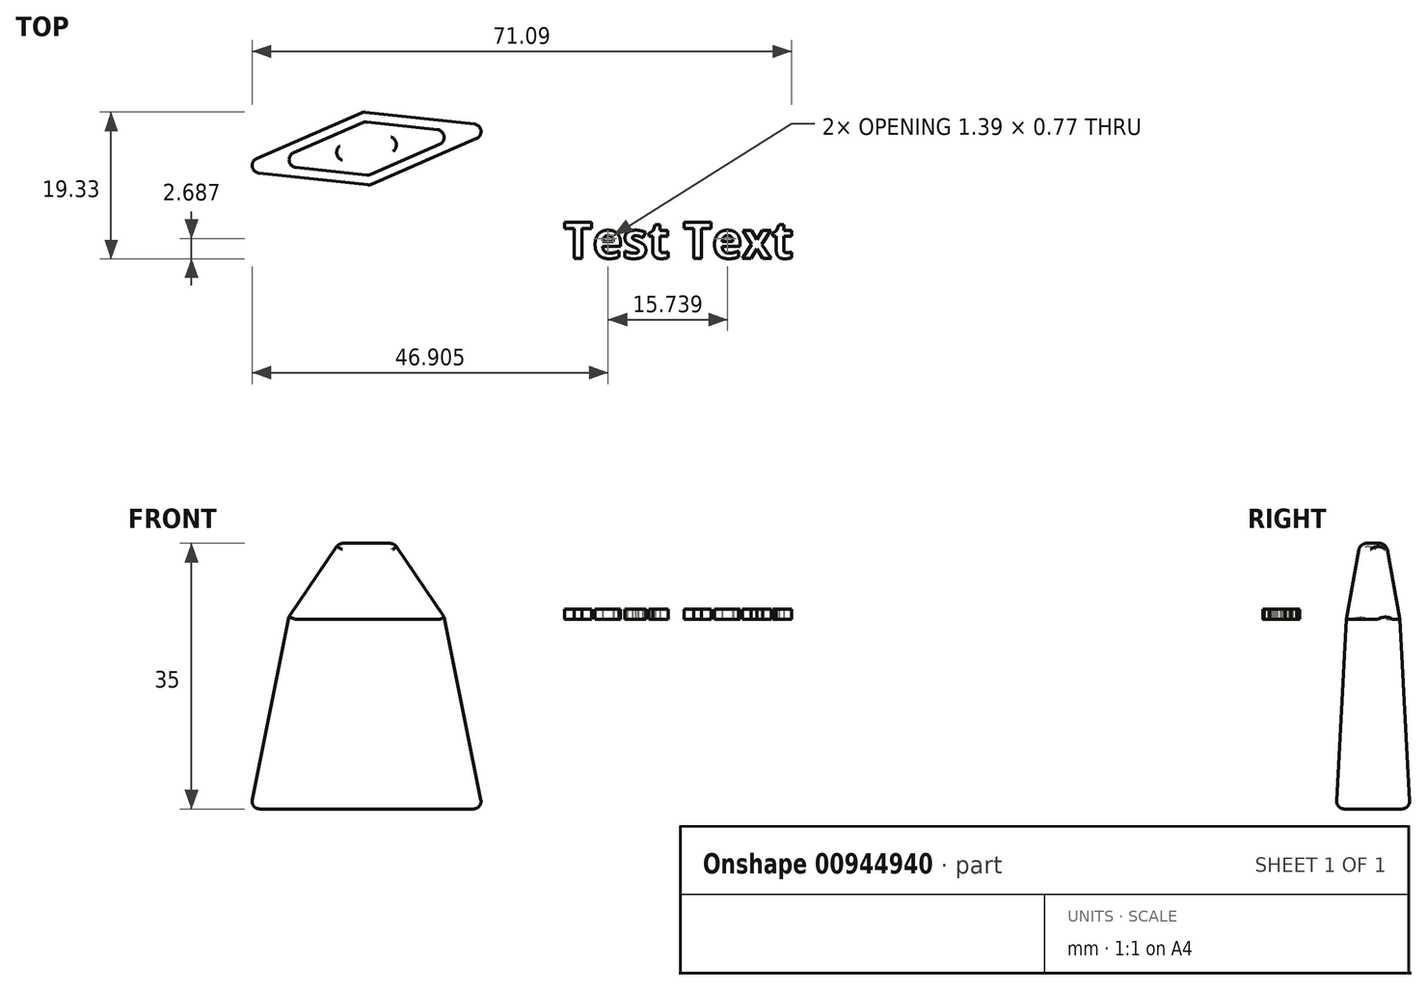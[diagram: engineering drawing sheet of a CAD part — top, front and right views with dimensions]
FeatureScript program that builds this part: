
annotation { "Feature Type Name" : "Feature", "Feature Type Description" : "" }
export const myFeature = defineFeature(function(context is Context, id is Id, definition is map)
    precondition{}
    {
        {
            var Q0;
            Q0=qCreatedBy(makeId("Top.planeOp"),FACE);
            var sketch = newSketch(context, id + "F0", { "sketchPlane" : qUnion([Q0])});
            skText(sketch, "E0", { "text": "Test Text", "fontName": "OpenSans-Bold.ttf"});
            const initialGuessF0  = {"E0": [0, 0, 1, 0, 0.0048]};
            skSetInitialGuess(sketch, initialGuessF0);
            skSolve(sketch);
        }
        {
            var Q0;
            Q0 = qSketchRegion(id + "F0", true);
            extrude(context, id + "F1", {"entities" : qUnion([Q0]), "depth" : 1.3 * mm, "offsetDistance" : 25 * mm});
        }
        {
            var Q0;
            Q0=qCreatedBy(makeId("Top.planeOp"),FACE);
            var sketch = newSketch(context, id + "F2", { "sketchPlane" : qUnion([Q0])});
            skLineSegment(sketch, "E1", {"start": v(-12.85, 16.54) * mm, "end": v(-26.18, 18) * mm});
            skLineSegment(sketch, "E2", {"start": v(-26.18, 18) * mm, "end": v(-39.04, 12.38) * mm});
            skLineSegment(sketch, "E3", {"start": v(-39.04, 12.38) * mm, "end": v(-25.7, 10.93) * mm});
            skLineSegment(sketch, "E4", {"start": v(-25.7, 10.93) * mm, "end": v(-12.85, 16.54) * mm});
            skSolve(sketch);
        }
        {
            var Q0;
            Q0 = qSketchRegion(id + "F2", true);
            var Q1;
            Q1=sQuery(id+"F2.wireOp",EDGE,"E3");
            var Q2;
            Q2=sQuery(id+"F2.wireOp",EDGE,"E4");
            var Q3;
            Q3=sQuery(id+"F2.wireOp",EDGE,"E1");
            var Q4;
            Q4=sQuery(id+"F2.wireOp",EDGE,"E2");
            extrude(context, id + "F3", {"entities" : qUnion([Q0]), "surfaceEntities" : qUnion([Q1, Q2, Q3, Q4]), "depth" : 10 * mm, "offsetDistance" : 25 * mm, "hasDraft" : true, "draftAngle" : 10 * degree, "draftPullDirection" : true, "hasSecondDirection" : true, "secondDirectionOppositeDirection" : true, "secondDirectionDepth" : 25 * mm, "hasSecondDirectionDraft" : true, "secondDirectionDraftAngle" : 3 * degree});
        }
        {
            var Q0;
            Q0=makeQuery(id+"F3.*.split.splitOp","SPLIT",EDGE,{"derivedFrom":makeQuery(id+"F3.opExtrude","SWEPT_EDGE",EDGE,{"disambiguationData":[OSD([sQuery(id+"F2.wireOp",EDGE,"E1"),sQuery(id+"F2.wireOp",EDGE,"E4")])]})});
            var Q1;
            Q1=makeQuery(id+"F3.*.split.splitOp","SPLIT",EDGE,{"derivedFrom":makeQuery(id+"F3.opExtrude","SWEPT_EDGE",EDGE,{"disambiguationData":[OSD([sQuery(id+"F2.wireOp",EDGE,"E2"),sQuery(id+"F2.wireOp",EDGE,"E3")])]})});
            var Q2;
            Q2=makeQuery(id+"F3.*.split.splitOp","SPLIT",EDGE,{"derivedFrom":makeQuery(id+"F3.opExtrude","SWEPT_EDGE",EDGE,{"disambiguationData":[OSD([sQuery(id+"F2.wireOp",EDGE,"E3"),sQuery(id+"F2.wireOp",EDGE,"E4")])]})});
            var Q3;
            Q3=makeQuery(id+"F3.*.split.splitOp","SPLIT",EDGE,{"derivedFrom":makeQuery(id+"F3.opExtrude","SWEPT_EDGE",EDGE,{"disambiguationData":[OSD([sQuery(id+"F2.wireOp",EDGE,"E1"),sQuery(id+"F2.wireOp",EDGE,"E2")])]})});
            var Q4;
            Q4=makeQuery(id+"F3.*.split.splitOp","SPLIT",EDGE,{"derivedFrom":makeQuery(id+"F3.opExtrude","SWEPT_EDGE",EDGE,{"disambiguationData":[OSD([sQuery(id+"F2.wireOp",EDGE,"E1"),sQuery(id+"F2.wireOp",EDGE,"E4")])]}),"isFromBackBody":true});
            var Q5;
            Q5=makeQuery(id+"F3.*.split.splitOp","SPLIT",EDGE,{"derivedFrom":makeQuery(id+"F3.opExtrude","SWEPT_EDGE",EDGE,{"disambiguationData":[OSD([sQuery(id+"F2.wireOp",EDGE,"E2"),sQuery(id+"F2.wireOp",EDGE,"E3")])]}),"isFromBackBody":true});
            var Q6;
            Q6=makeQuery(id+"F3.opExtrude","CAP_EDGE",EDGE,{"disambiguationData":[OSD([sQuery(id+"F2.wireOp",EDGE,"E3")])],"isStart":true});
            var Q7;
            Q7=makeQuery(id+"F3.opExtrude","CAP_EDGE",EDGE,{"disambiguationData":[OSD([sQuery(id+"F2.wireOp",EDGE,"E4")])],"isStart":true});
            var Q8;
            Q8=makeQuery(id+"F3.opExtrude","CAP_EDGE",EDGE,{"disambiguationData":[OSD([sQuery(id+"F2.wireOp",EDGE,"E1")])],"isStart":true});
            var Q9;
            Q9=makeQuery(id+"F3.opExtrude","CAP_EDGE",EDGE,{"disambiguationData":[OSD([sQuery(id+"F2.wireOp",EDGE,"E2")])],"isStart":true});
            var Q10;
            Q10=makeQuery(id+"F3.*.split.splitOp","SPLIT",EDGE,{"derivedFrom":makeQuery(id+"F3.opExtrude","SWEPT_EDGE",EDGE,{"disambiguationData":[OSD([sQuery(id+"F2.wireOp",EDGE,"E3"),sQuery(id+"F2.wireOp",EDGE,"E4")])]}),"isFromBackBody":true});
            var Q11;
            Q11=makeQuery(id+"F3.*.split.splitOp","SPLIT",EDGE,{"derivedFrom":makeQuery(id+"F3.opExtrude","SWEPT_EDGE",EDGE,{"disambiguationData":[OSD([sQuery(id+"F2.wireOp",EDGE,"E1"),sQuery(id+"F2.wireOp",EDGE,"E2")])]}),"isFromBackBody":true});
            var Q12;
            Q12=makeQuery(id+"F3.opExtrude","CAP_EDGE",EDGE,{"disambiguationData":[OSD([sQuery(id+"F2.wireOp",EDGE,"E2")])],"isStart":false});
            var Q13;
            Q13=makeQuery(id+"F3.opExtrude","CAP_EDGE",EDGE,{"disambiguationData":[OSD([sQuery(id+"F2.wireOp",EDGE,"E1")])],"isStart":false});
            var Q14;
            Q14=makeQuery(id+"F3.opExtrude","CAP_EDGE",EDGE,{"disambiguationData":[OSD([sQuery(id+"F2.wireOp",EDGE,"E3")])],"isStart":false});
            var Q15;
            Q15=makeQuery(id+"F3.opExtrude","CAP_EDGE",EDGE,{"disambiguationData":[OSD([sQuery(id+"F2.wireOp",EDGE,"E4")])],"isStart":false});
            fillet(context, id + "F4", {"entities" : qUnion([Q0, Q1, Q2, Q3, Q4, Q5, Q6, Q7, Q8, Q9, Q10, Q11, Q12, Q13, Q14, Q15]), "radius" : 1 * mm, "tangentPropagation" : true, "allowEdgeOverflow" : false});
        }
    });
